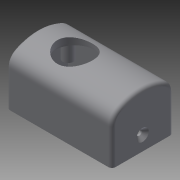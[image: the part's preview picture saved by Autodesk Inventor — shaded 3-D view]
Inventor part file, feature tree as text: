
AUTODESK INVENTOR PART (.ipt)
format: ipt  version: 2014 (Build 180170000, 170)  size: 239,616 bytes
history: native  units: mm
features: sketch x8, extrude x7, projected_geometry x4, fillet x2, chamfer x1
ambient origin geometry x8: Origin, YZ Plane, XZ Plane, XY Plane, X Axis, Y Axis, Z Axis, Center Point
bodies: Solid1 (feature_tree)
feature tree (22):
  extrude  "Extrusion1"  Depth=60.0mm
  extrude  "Extrusion2"  Depth=3.0mm
  fillet  "Fillet1"  Radius=25.0mm
  extrude  "Extrusion3"  Depth=9.0mm
  fillet  "Fillet2"  Radius=20.0mm
  extrude  "Extrusion4"  Depth=2.0mm
  extrude  "Extrusion5"  Depth=2.0mm
  extrude  "Extrusion6"  Depth=2.5mm
  chamfer  "Chamfer1"  Distance=2.5mm
  sketch  "Sketch7"  dims[d19=2.5mm d20=6.0mm d21=2.5mm d22=6.0mm d23=3.0mm]
  extrude  "Extrusion7"  Depth=2.5mm
  sketch  "Sketch1"  dims[d0=60.0mm d1=35.0mm]
  sketch  "Sketch2"  dims[d2=3.0mm d3=3.0mm d4=25.0mm d5=0.0mm]
  sketch  "Sketch3"  dims[d6=25.0mm d7=0.0mm d8=9.0mm d9=20.0mm]
  sketch  "Sketch4"  dims[d10=25.0mm d11=0.0mm d12=2.0mm]
  projected_geometry  "Projected Loop1"
  sketch  "Sketch5"  dims[d13=2.0mm d14=2.0mm]
  projected_geometry  "Projected Loop2"
  projected_geometry  "Projected Loop3"
  projected_geometry  "Projected Loop4"
  sketch  "Sketch6"  dims[d15=2.5mm d16=6.0mm d17=2.5mm d18=6.0mm]
  sketch  "Sketch8"  dims[d24=3.0mm d25=3.0mm d26=3.0mm d27=3.0mm d28=3.0mm d29=3.0mm d30=3.0mm d31=10.0mm d32=0.0mm d33=3.0mm d34=0.0mm d35=3.0mm d36=3.0mm d37=0.0mm d38=2.0mm d39=2.0mm d40=45.0deg d41=18.4mm d42=14.5mm d43=18.4mm d44=8.6mm d45=8.2mm d46=23.0mm d47=2.0mm d48=0.0mm]
